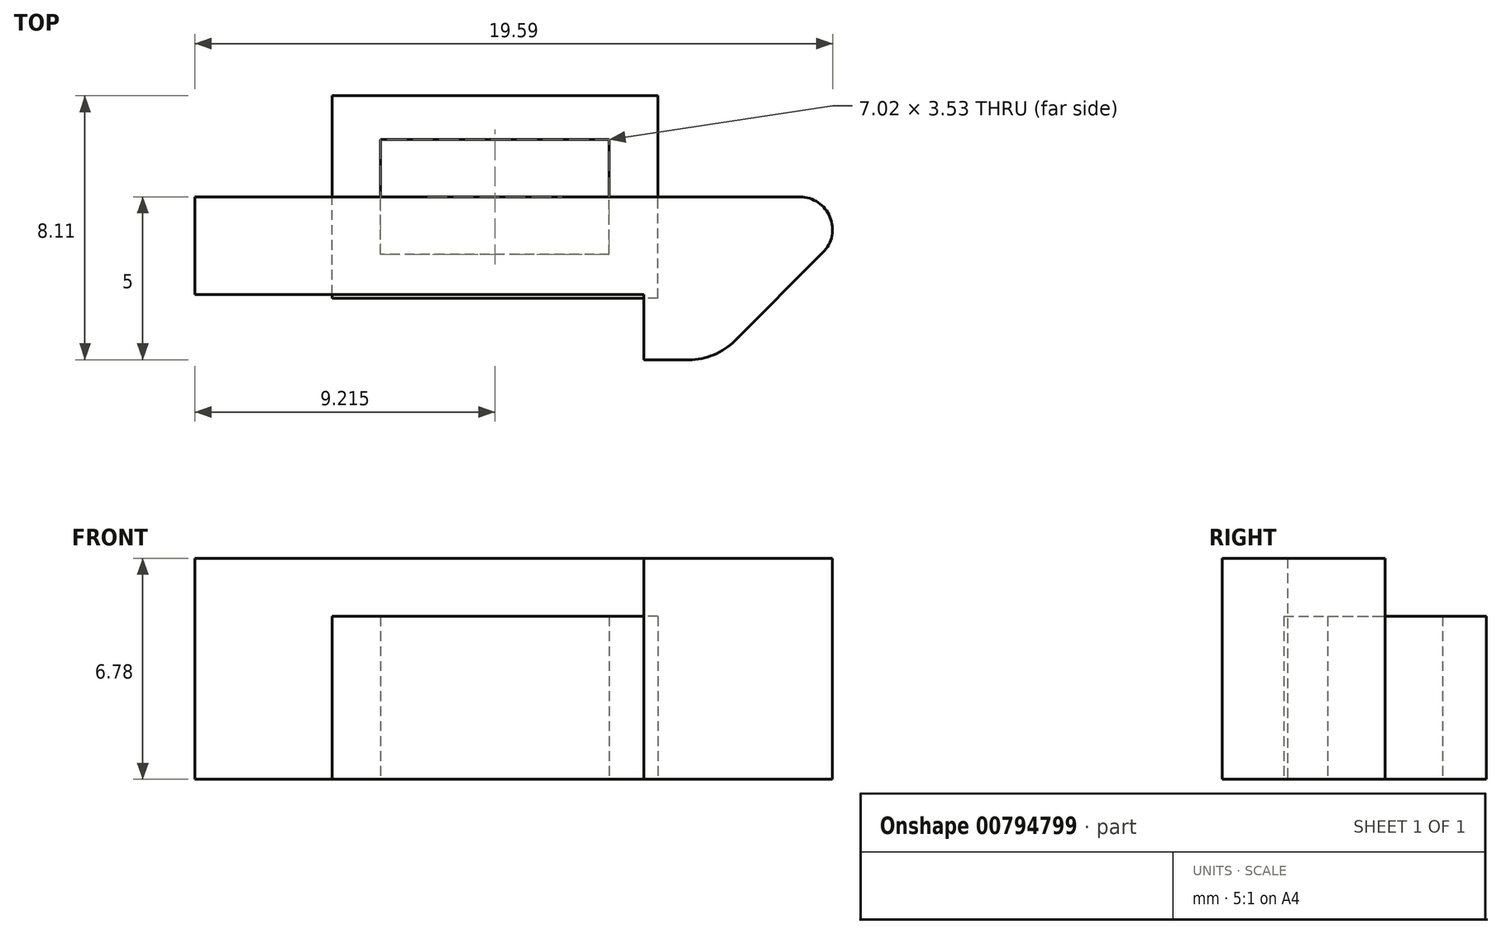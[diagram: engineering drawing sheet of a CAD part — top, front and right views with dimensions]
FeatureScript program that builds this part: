
annotation { "Feature Type Name" : "Feature", "Feature Type Description" : "" }
export const myFeature = defineFeature(function(context is Context, id is Id, definition is map)
    precondition{}
    {
        {
            var Q0;
            Q0=qCreatedBy(makeId("Front.planeOp"),FACE);
            var sketch = newSketch(context, id + "F0", { "sketchPlane" : qUnion([Q0])});
            skLineSegment(sketch, "E0", {"start": v(0, 0) * mm, "end": v(20, 0) * mm});
            skLineSegment(sketch, "E1", {"start": v(20, 0) * mm, "end": v(20, 6.78) * mm});
            skLineSegment(sketch, "E2", {"start": v(20, 6.78) * mm, "end": v(0, 6.78) * mm});
            skLineSegment(sketch, "E3", {"start": v(0, 6.78) * mm, "end": v(0, 0) * mm});
            skLineSegment(sketch, "E4", {"start": v(13.8, 6.78) * mm, "end": v(13.8, 0) * mm});
            skSolve(sketch);
        }
        {
            var Q0;
            {var subQ0=sQuery(id+"F0.wireOp",EDGE,"E1");Q0=makeQuery(id+"F0.imprint","IMPRINT",FACE,{"disambiguationData":[TD([[makeQuery(id+"F0.imprint","IMPRINT",EDGE,{"derivedFrom":subQ0}),1.0]])]});}
            extrude(context, id + "F1", {"entities" : qUnion([Q0]), "depth" : 5 * mm, "offsetDistance" : 25 * mm});
        }
        {
            var Q0;
            {var subQ0=sQuery(id+"F0.wireOp",EDGE,"E3");Q0=makeQuery(id+"F0.imprint","IMPRINT",FACE,{"disambiguationData":[TD([[makeQuery(id+"F0.imprint","IMPRINT",EDGE,{"derivedFrom":subQ0}),1.0]])]});}
            var Q1;
            Q1=qSketchRegion(id+"F0",true);
            extrude(context, id + "F2", {"entities" : qUnion([Q0, Q1]), "operationType" : NewBodyOperationType.ADD, "depth" : 3 * mm, "offsetDistance" : 25 * mm});
        }
        {
            var Q0;
            Q0=makeQuery(id+"F1.opExtrude","CAP_EDGE",EDGE,{"disambiguationData":[OSD([sQuery(id+"F0.wireOp",EDGE,"E1")])],"isStart":false});
            chamfer(context, id + "F3", {"entities" : qUnion([Q0]), "width" : 4 * mm, "tangentPropagation" : true});
        }
        {
            var Q0;
            Q0=makeQuery(id+"F1.opExtrude","CAP_EDGE",EDGE,{"disambiguationData":[OSD([sQuery(id+"F0.wireOp",EDGE,"E1")])],"isStart":true});
            fillet(context, id + "F4", {"entities" : qUnion([Q0]), "radius" : 1.46 * mm, "tangentPropagation" : true, "allowEdgeOverflow" : false});
        }
        {
            var Q0;
            {var subQ0=sQuery(id+"F0.wireOp",EDGE,"E1");Q0=makeQuery(id+"F4.opFillet","BLEND_EDGE",EDGE,{"blendedFrom":[makeQuery(id+"F1.opExtrude","CAP_EDGE",EDGE,{"disambiguationData":[OSD([subQ0])],"isStart":true}),makeQuery(id+"F3.opChamfer","BLEND_FACE",FACE,{"disambiguationData":[OSD([subQ0])]})],"blendedInto":[makeQuery(id+"F3.opChamfer","BLEND_FACE",FACE,{"disambiguationData":[OSD([subQ0])]})]});}
            fillet(context, id + "F5", {"entities" : qUnion([Q0]), "radius" : 1 * mm, "tangentPropagation" : true, "allowEdgeOverflow" : false});
        }
        {
            var Q0;
            {var subQ0=sQuery(id+"F0.wireOp",EDGE,"E1");Q0=makeQuery(id+"F3.opChamfer","BLEND_EDGE",EDGE,{"blendedFrom":[makeQuery(id+"F1.opExtrude","CAP_EDGE",EDGE,{"disambiguationData":[OSD([subQ0])],"isStart":false}),makeQuery(id+"F1.opExtrude","CAP_FACE",FACE,{"disambiguationData":[OSD([sQuery(id+"F0.wireOp",EDGE,"E0"),subQ0,sQuery(id+"F0.wireOp",EDGE,"E2"),sQuery(id+"F0.wireOp",EDGE,"E4")])],"isStart":false})],"blendedInto":[makeQuery(id+"F1.opExtrude","CAP_FACE",FACE,{"disambiguationData":[OSD([sQuery(id+"F0.wireOp",EDGE,"E0"),subQ0,sQuery(id+"F0.wireOp",EDGE,"E2"),sQuery(id+"F0.wireOp",EDGE,"E4")])],"isStart":false})]});}
            fillet(context, id + "F6", {"entities" : qUnion([Q0]), "radius" : 2 * mm, "tangentPropagation" : true, "allowEdgeOverflow" : false});
        }
        {
            var Q0;
            {var subQ0=sQuery(id+"F0.wireOp",EDGE,"E3");Q0=makeQuery(id+"F0.imprint","IMPRINT",FACE,{"disambiguationData":[TD([[makeQuery(id+"F0.imprint","IMPRINT",EDGE,{"derivedFrom":subQ0}),1.0]])]});}
            var sketch = newSketch(context, id + "F7", { "sketchPlane" : qUnion([Q0])});
            skLineSegment(sketch, "E5.bottom", {"start": v(13.83, 6.72) * mm, "end": v(6.6, 6.72) * mm});
            skLineSegment(sketch, "E5.top", {"start": v(13.83, 0) * mm, "end": v(6.6, 0) * mm});
            skLineSegment(sketch, "E5.left", {"start": v(13.83, 6.72) * mm, "end": v(13.83, 0) * mm});
            skLineSegment(sketch, "E5.right", {"start": v(6.6, 6.72) * mm, "end": v(6.6, 0) * mm});
            skSolve(sketch);
        }
        {
            var Q0;
            {var subQ0=sQuery(id+"F7.wireOp",EDGE,"E5.right");Q0=makeQuery(id+"F7.imprint","IMPRINT",FACE,{"disambiguationData":[TD([[makeQuery(id+"F7.imprint","IMPRINT",EDGE,{"derivedFrom":subQ0}),1.0]])]});}
            extrude(context, id + "F8", {"entities" : qUnion([Q0]), "depth" : 25 * mm, "offsetDistance" : 25 * mm});
        }
        {
            var Q0;
            Q0=makeQuery(id+"F8.opExtrude","SWEPT_BODY",BODY,{"disambiguationData":[OSD([sQuery(id+"F0.wireOp",EDGE,"E4"),sQuery(id+"F7.wireOp",EDGE,"E5.bottom"),sQuery(id+"F7.wireOp",EDGE,"E5.top"),sQuery(id+"F7.wireOp",EDGE,"E5.right")])]});
            deleteBodies(context, id + "F9", {"entities" : qUnion([Q0])});
        }
        {
            var Q0;
            Q0=qCreatedBy(makeId("Top.planeOp"),FACE);
            var sketch = newSketch(context, id + "F10", { "sketchPlane" : qUnion([Q0])});
            skLineSegment(sketch, "E6.bottom", {"start": v(12.73, -1.77) * mm, "end": v(5.7, -1.77) * mm});
            skLineSegment(sketch, "E6.top", {"start": v(12.73, 1.77) * mm, "end": v(5.7, 1.77) * mm});
            skLineSegment(sketch, "E6.left", {"start": v(12.73, -1.77) * mm, "end": v(12.73, 1.77) * mm});
            skLineSegment(sketch, "E6.right", {"start": v(5.7, -1.77) * mm, "end": v(5.7, 1.77) * mm});
            skPoint(sketch, "E6.middle", {"position": v(9.21, 0) * mm});
            skLineSegment(sketch, "E7.bottom", {"start": v(14.21, -3.1) * mm, "end": v(4.21, -3.1) * mm});
            skLineSegment(sketch, "E7.top", {"start": v(14.21, 3.1) * mm, "end": v(4.21, 3.1) * mm});
            skLineSegment(sketch, "E7.left", {"start": v(14.21, -3.1) * mm, "end": v(14.21, 3.1) * mm});
            skLineSegment(sketch, "E7.right", {"start": v(4.21, -3.1) * mm, "end": v(4.21, 3.1) * mm});
            skSolve(sketch);
        }
        {
            var Q0;
            Q0=makeQuery(id+"F10.imprint","IMPRINT",FACE,{"disambiguationData":[TD([[makeQuery(id+"F10.imprint","IMPRINT",EDGE,{"derivedFrom":sQuery(id+"F10.wireOp",EDGE,"E6.bottom")}),1.0]])]});
            extrude(context, id + "F11", {"entities" : qUnion([Q0]), "depth" : 5 * mm, "offsetDistance" : 25 * mm});
        }
    });
